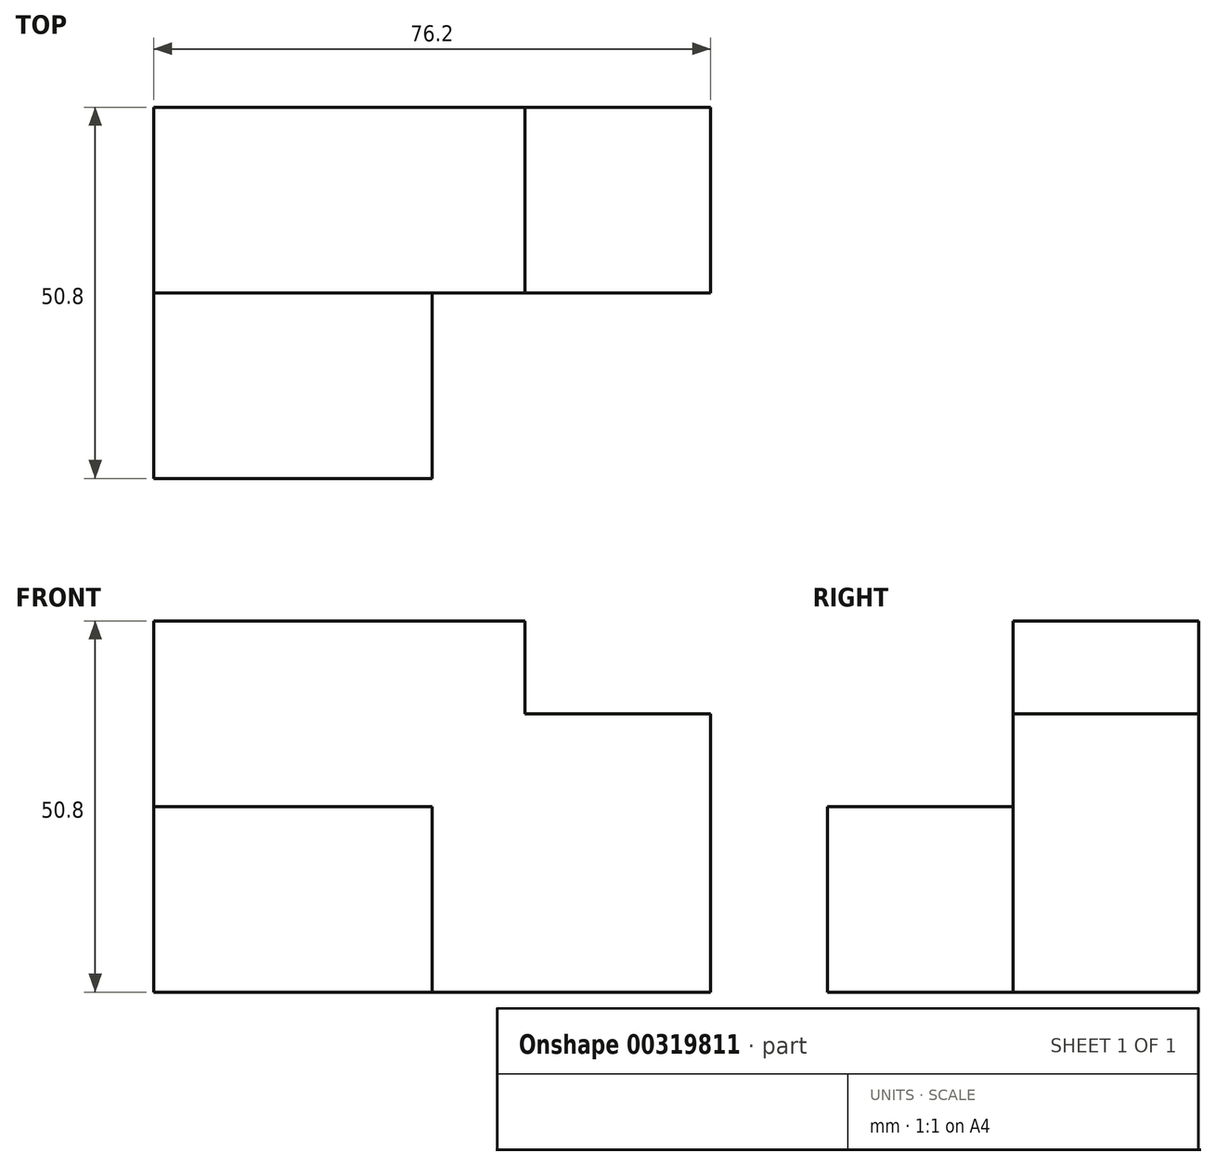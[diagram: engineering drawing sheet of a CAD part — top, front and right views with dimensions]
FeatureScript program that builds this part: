
annotation { "Feature Type Name" : "Feature", "Feature Type Description" : "" }
export const myFeature = defineFeature(function(context is Context, id is Id, definition is map)
    precondition{}
    {
        {
            var Q0;
            Q0=qCreatedBy(makeId("Front.planeOp"),FACE);
            var sketch = newSketch(context, id + "F0", { "sketchPlane" : qUnion([Q0])});
            skLineSegment(sketch, "E0.bottom", {"start": v(-35.12, 22.52) * mm, "end": v(41.08, 22.52) * mm});
            skLineSegment(sketch, "E0.top", {"start": v(-35.12, -28.28) * mm, "end": v(41.08, -28.28) * mm});
            skLineSegment(sketch, "E0.left", {"start": v(-35.12, 22.52) * mm, "end": v(-35.12, -28.28) * mm});
            skLineSegment(sketch, "E0.right", {"start": v(41.08, 22.52) * mm, "end": v(41.08, -28.28) * mm});
            skSolve(sketch);
        }
        {
            var Q0;
            Q0=makeQuery(id+"F0.imprint","IMPRINT",FACE,{"disambiguationData":[TD([[makeQuery(id+"F0.imprint","IMPRINT",EDGE,{"derivedFrom":sQuery(id+"F0.wireOp",EDGE,"E0.bottom")}),-1.0]])]});
            extrude(context, id + "F1", {"entities" : qUnion([Q0]), "oppositeDirection" : true, "depth" : 25.4 * mm});
        }
        {
            var Q0;
            Q0=makeQuery(id+"F1.opExtrude","CAP_FACE",FACE,{"disambiguationData":[OSD([sQuery(id+"F0.wireOp",EDGE,"E0.bottom"),sQuery(id+"F0.wireOp",EDGE,"E0.top"),sQuery(id+"F0.wireOp",EDGE,"E0.left"),sQuery(id+"F0.wireOp",EDGE,"E0.right")])],"isStart":true});
            var sketch = newSketch(context, id + "F2", { "sketchPlane" : qUnion([Q0])});
            skLineSegment(sketch, "E1", {"start": v(-35.12, -28.28) * mm, "end": v(2.98, -28.28) * mm});
            skLineSegment(sketch, "E2", {"start": v(2.98, -28.28) * mm, "end": v(2.98, -2.88) * mm});
            skLineSegment(sketch, "E3", {"start": v(2.98, -2.88) * mm, "end": v(-35.12, -2.88) * mm});
            skLineSegment(sketch, "E4", {"start": v(-35.12, -2.88) * mm, "end": v(-35.12, -28.28) * mm});
            skLineSegment(sketch, "E5", {"start": v(41.08, 9.82) * mm, "end": v(15.68, 9.82) * mm});
            skLineSegment(sketch, "E6", {"start": v(15.68, 9.82) * mm, "end": v(15.68, 22.52) * mm});
            skLineSegment(sketch, "E7", {"start": v(15.68, 22.52) * mm, "end": v(41.08, 22.52) * mm});
            skLineSegment(sketch, "E8", {"start": v(41.08, 22.52) * mm, "end": v(41.08, 9.82) * mm});
            skSolve(sketch);
        }
        {
            var Q0;
            Q0=makeQuery(id+"F2.imprint","IMPRINT",FACE,{"disambiguationData":[TD([[makeQuery(id+"F2.imprint","IMPRINT",EDGE,{"derivedFrom":sQuery(id+"F2.wireOp",EDGE,"E1")}),1.0]])]});
            extrude(context, id + "F3", {"entities" : qUnion([Q0]), "operationType" : NewBodyOperationType.ADD, "depth" : 25.4 * mm});
        }
        {
            var Q0;
            Q0=makeQuery(id+"F2.imprint","IMPRINT",FACE,{"disambiguationData":[TD([[makeQuery(id+"F2.imprint","IMPRINT",EDGE,{"derivedFrom":sQuery(id+"F2.wireOp",EDGE,"E5")}),-1.0]])]});
            extrude(context, id + "F4", {"entities" : qUnion([Q0]), "operationType" : NewBodyOperationType.REMOVE, "oppositeDirection" : true, "depth" : 25.4 * mm});
        }
    });
